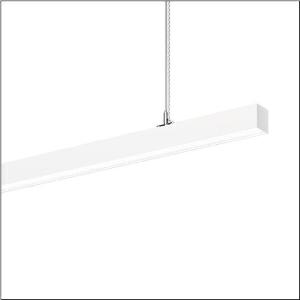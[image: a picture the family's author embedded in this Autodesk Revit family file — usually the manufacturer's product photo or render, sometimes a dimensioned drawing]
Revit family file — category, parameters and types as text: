
# Revit family: silica_r__21_51mx30db45wb_134d
name_source: partatom
category: Lighting Fixtures
units: mm (PartAtom-declared; Revit-internal decimal feet)

## family parameters
Cut with Voids When Loaded = No
Host = Face
Light Source = No
Part Type = Normal
Room Calculation Point = No
Round Connector Dimension = Use Diameter
Shared = No

## types (1)
- --- (1 x LED, 5260 lm, 32 W, 4000K)
    Apparent Load = 32 VA
    CIE Flux Codes = 47 79 96 57 100
    Color Rendering = 80
    Color Temperature = 4000K
    Default Elevation = 1800 mm
    Description = Silica® 21, office luminaire, primary optical cover: cover, of PMMA, opal, light emission: direct/indirect distribution, primary light characteristic: symmetric, installation type: suspended mounting, LED, rated luminous flux: 5.260lm, luminous efficacy: 164lm/W, light colour: 840, colour temperature: 4000K, with terminal, 3+2-pole, max. 2.5mm², mains connection: 220..240V, AC, 50/60Hz, rated input power: 32W, luminaire housing, of aluminium, traffic white (RAL 9016), length: 1.504mm, width: 53mm, height: 53mm, protection rating (complete): IP20, insulation class (complete): insulation class I (protective earthing), certification: CE, permissible operating ambient temperature: 0..+35°C, standard: EN 50419, packaging unit: 1 piece
    Height = 53 mm
    Lamp = 1 x LED
    Lamp Light Flux = 5260 lm
    Lamp Power = 32 W
    Lamp count = 1
    Length = 1504 mm
    Luminous efficacy = 164 lm/W
    Manufacturer = Siteco
    ModVariant = No
    Model = 51MX30DB45WB
    Mounting Place = Ceiling
    Mounting Type = Pendant
    Number of Poles = 1
    OnlyDefault = Yes
    Power Factor = 1
    Product Name = Silica® 21
    Product group = office luminaire | ceiling pendant
    ProductGroupID = 902
    Protection Class = Protection class I
    Protection Degree = IP 20
    RLX_Detail_Level = 1
    RLX_Emergency_Light_Flux = 0 lm
    RLX_Emergency_Type = 0
    RLX_Emergency_Type_DB = No
    RlxData = <blob elided: 21233 chars, md5=c6ed1685>
    Socket = socket
    Standby Power = 0 W
    System Light Flux = 5260 lm
    System Power = 32 W
    Type Comments = factory setting: luminous flux: 100 % | dim-lin: 254 | 218 mA
    Type Image = l_1297784.jpg
    URL = http://relux.com
    VarID = @adj_046849
    Voltage = 0 V
    Weight = 0.00 kg
    Width = 53 mm

## geometry (parser evidence)
native form markers: Blend x4, Sweep x13
no freeform markers — native parametric forms only
